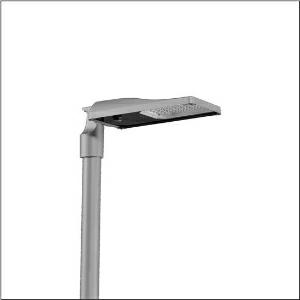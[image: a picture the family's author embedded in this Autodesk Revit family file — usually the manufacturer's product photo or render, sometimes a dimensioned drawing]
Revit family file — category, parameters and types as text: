
# Revit family: streetlight_sl_31_mini___st1_0a_5xh2d31r08ja_e878
name_source: partatom
category: Lighting Fixtures
units: mm (PartAtom-declared; Revit-internal decimal feet)

## family parameters
Cut with Voids When Loaded = No
Host = Face
Light Source = No
Part Type = Normal
Room Calculation Point = No
Round Connector Dimension = Use Diameter
Shared = No

## types (1)
- --- (1 x LED, 12270 lm, 82.5 W, 3000K)
    Apparent Load = 83 VA
    CIE Flux Codes = 40 73 97 100 100
    Color Rendering = 70
    Color Temperature = 3000K
    Default Elevation = 1800 mm
    Description = Streetlight SL 31 mini D4i, Desk-Remote mast luminaire for post-top, side-entry; light control with lens of PMMA; light distribution: ST1.0a, direct asymmetric distribution, for standard-compliant lighting for roads and squares; LED: luminous flux: 12.270lm, light colour: 730, colour temperature: 3000K; luminous efficacy: 148,7lm/W; control: pre-setting: logarithmic dimming characteristic, flexible luminous flux parameterisation, time-dependent luminous flux control, constant luminous flux control, power reduction, intelligent temperature release in ECG and LED module, overheat protection; luminaire housing, of diecast aluminium, Siteco® metallic grey (DB 702S), corrosivity category C5 high according to DIN EN ISO 12944; cover of toughened safety glass, transparent, mast flange of diecast aluminium, Siteco® metallic grey (DB 702S), spigot size: 76/60mm, mast flange included unmounted; with cable H07RN-F 2x 1.5mm², cable length: 10,5m, connection cable pre-assembled; mains connection: 220..240V, AC, 50/60Hz; power consumption (at start of service life): 82,5W / (at end of service life): 90,1W / (with reduced operation 50%): 36,8W; protection rating (complete): IP66; insulation class (complete): insulation class II (safety insulation); impact resistance: IK09; certification: CE, ENEC, ENEC+, VDE, UKCA, ZD4i; permissible operating ambient temperature for outdoor applications: -40..+50°C; packaging unit: 1 piece

Light Distribution: ST1.0a
    Height = 76 mm
    Lamp = 1 x LED
    Lamp Light Flux = 12270 lm
    Lamp Power = 82.5 W
    Lamp count = 1
    Length = 547 mm
    Luminous efficacy = 149 lm/W
    Manufacturer = Siteco
    ModVariant = No
    Model = 5XH2D31R08JA
    Number of Poles = 1
    OnlyDefault = Yes
    Power Factor = 1
    Product Name = Streetlight SL 31 mini | ST1.0a
    Product group = mast luminaire | pylon top
    ProductGroupID = 6100
    Protection Class = Protection class II
    Protection Degree = IP 66
    RLX_Detail_Level = 1
    RLX_Emergency_Light_Flux = 0 lm
    RLX_Emergency_Type = 0
    RLX_Emergency_Type_DB = No
    RlxData = <blob elided: 39753 chars, md5=6deed980>
    Socket = socket
    Standby Power = 0 W
    System Light Flux = 12270 lm
    System Power = 83 W
    Type Comments = factory setting: luminous flux: 100 % | dim-lin: 254 | 870 mA
    Type Image = l_1300328.jpg
    URL = http://relux.com
    VarID = @adj_071477
    Voltage = 0 V
    Weight = 0.00 kg
    Width = 265 mm

## geometry (parser evidence)
native form markers: Blend x4, Sweep x9
no freeform markers — native parametric forms only
